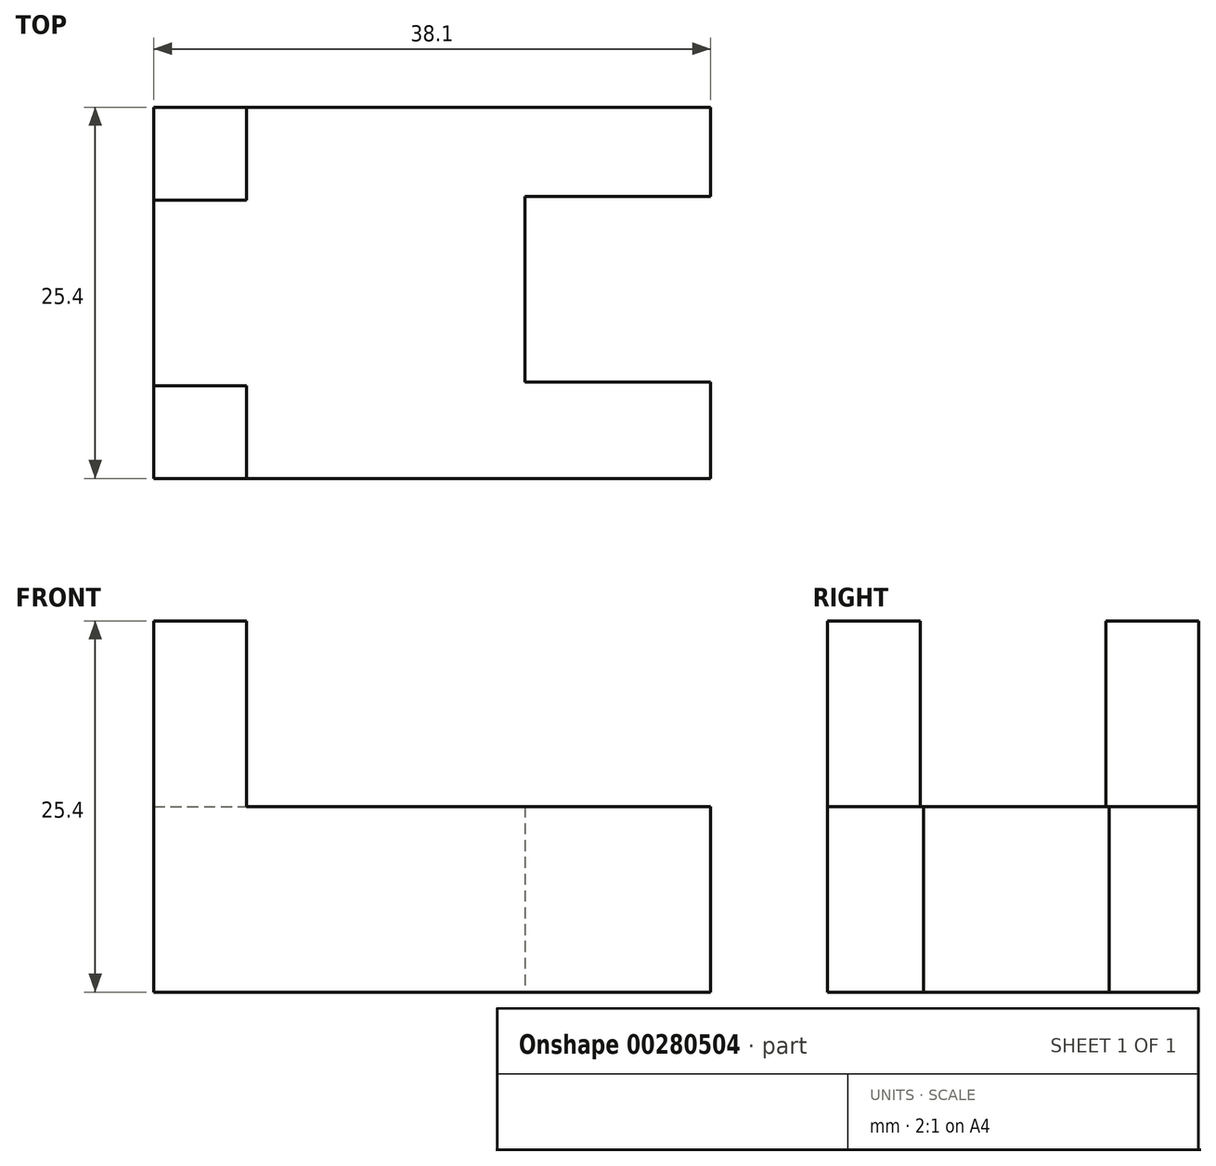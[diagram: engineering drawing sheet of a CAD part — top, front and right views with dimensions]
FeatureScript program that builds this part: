
annotation { "Feature Type Name" : "Feature", "Feature Type Description" : "" }
export const myFeature = defineFeature(function(context is Context, id is Id, definition is map)
    precondition{}
    {
        {
            var Q0;
            Q0=qCreatedBy(makeId("Front.planeOp"),FACE);
            var sketch = newSketch(context, id + "F0", { "sketchPlane" : qUnion([Q0])});
            skLineSegment(sketch, "E0", {"start": v(0, 0) * mm, "end": v(0, 25.4) * mm});
            skLineSegment(sketch, "E1", {"start": v(0, 25.4) * mm, "end": v(6.35, 25.4) * mm});
            skLineSegment(sketch, "E2", {"start": v(6.35, 25.4) * mm, "end": v(6.35, 12.7) * mm});
            skLineSegment(sketch, "E3", {"start": v(6.35, 12.7) * mm, "end": v(38.1, 12.7) * mm});
            skLineSegment(sketch, "E4", {"start": v(38.1, 12.7) * mm, "end": v(38.1, 0) * mm});
            skLineSegment(sketch, "E5", {"start": v(38.1, 0) * mm, "end": v(0, 0) * mm});
            skSolve(sketch);
        }
        {
            var Q0;
            Q0 = qSketchRegion(id + "F0", true);
            extrude(context, id + "F1", {"entities" : qUnion([Q0]), "depth" : 25.4 * mm});
        }
        {
            var Q0;
            Q0=makeQuery(id+"F1.opExtrude","SWEPT_FACE",FACE,{"disambiguationData":[OSD([sQuery(id+"F0.wireOp",EDGE,"E2")])]});
            var sketch = newSketch(context, id + "F2", { "sketchPlane" : qUnion([Q0])});
            skLineSegment(sketch, "E6", {"start": v(-19.05, 25.4) * mm, "end": v(-19.05, 12.7) * mm});
            skLineSegment(sketch, "E7", {"start": v(-19.05, 12.7) * mm, "end": v(-6.35, 12.7) * mm});
            skLineSegment(sketch, "E8", {"start": v(-6.35, 12.7) * mm, "end": v(-6.35, 25.4) * mm});
            skLineSegment(sketch, "E9", {"start": v(-6.35, 25.4) * mm, "end": v(-19.05, 25.4) * mm});
            skSolve(sketch);
        }
        {
            var Q0;
            Q0=makeQuery(id+"F2.imprint","IMPRINT",FACE,{"disambiguationData":[TD([[makeQuery(id+"F2.imprint","IMPRINT",EDGE,{"derivedFrom":sQuery(id+"F2.wireOp",EDGE,"E6")}),1.0]])]});
            extrude(context, id + "F3", {"entities" : qUnion([Q0]), "operationType" : NewBodyOperationType.REMOVE, "oppositeDirection" : true, "depth" : 25.4 * mm});
        }
        {
            var Q0;
            Q0=makeQuery(id+"F1.opExtrude","SWEPT_FACE",FACE,{"disambiguationData":[OSD([sQuery(id+"F0.wireOp",EDGE,"E4")])]});
            var sketch = newSketch(context, id + "F4", { "sketchPlane" : qUnion([Q0])});
            skLineSegment(sketch, "E10", {"start": v(-18.82, 12.7) * mm, "end": v(-18.82, 0) * mm});
            skLineSegment(sketch, "E11", {"start": v(-18.82, 0) * mm, "end": v(-6.12, 0) * mm});
            skLineSegment(sketch, "E12", {"start": v(-6.12, 0) * mm, "end": v(-6.12, 12.7) * mm});
            skLineSegment(sketch, "E13", {"start": v(-6.12, 12.7) * mm, "end": v(-18.82, 12.7) * mm});
            skSolve(sketch);
        }
        {
            var Q0;
            Q0 = qSketchRegion(id + "F4", true);
            extrude(context, id + "F5", {"entities" : qUnion([Q0]), "operationType" : NewBodyOperationType.REMOVE, "oppositeDirection" : true, "depth" : 12.7 * mm});
        }
    });
